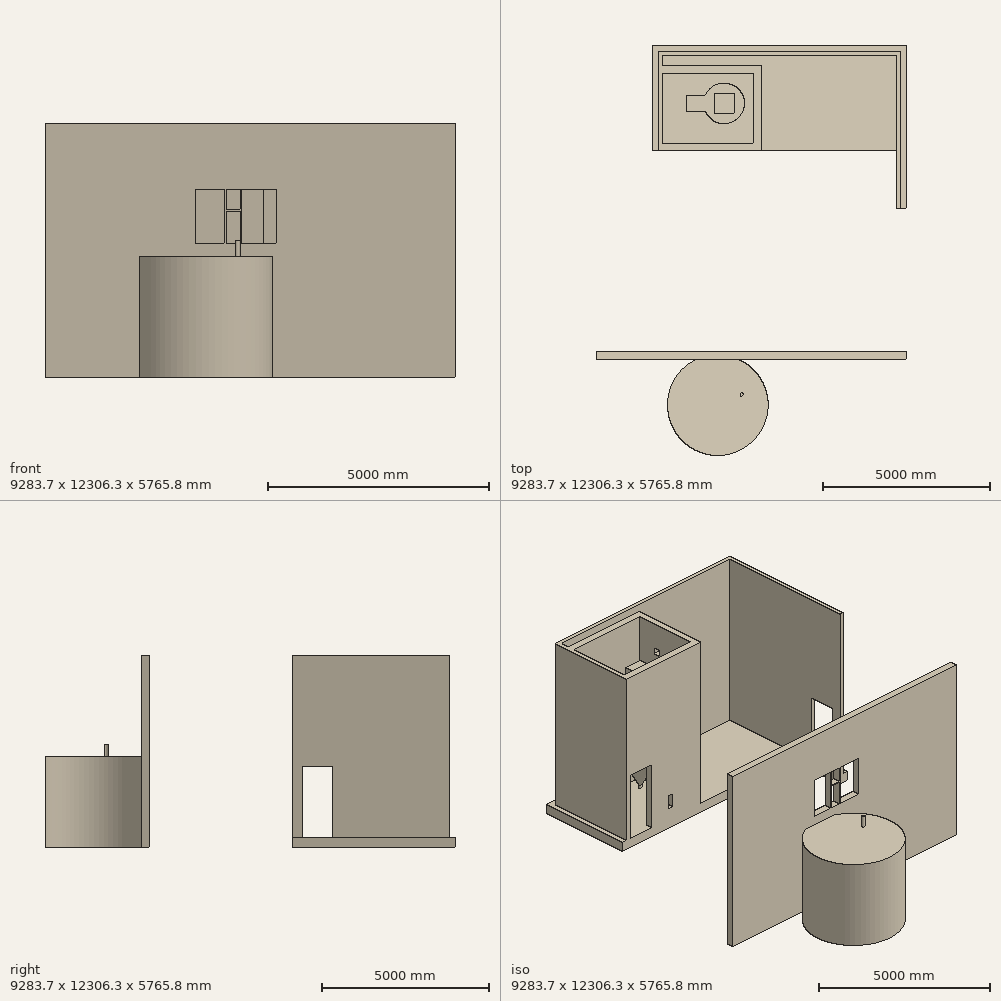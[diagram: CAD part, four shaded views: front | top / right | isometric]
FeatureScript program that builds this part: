
annotation { "Feature Type Name" : "Feature", "Feature Type Description" : "" }
export const myFeature = defineFeature(function(context is Context, id is Id, definition is map)
    precondition{}
    {
        {
            var Q0;
            Q0=qCreatedBy(makeId("Top.planeOp"),FACE);
            var sketch = newSketch(context, id + "F0", { "sketchPlane" : qUnion([Q0])});
            skLineSegment(sketch, "E0.bottom", {"start": v(-3263.9, 3149.6) * mm, "end": v(4051.3, 3149.6) * mm});
            skLineSegment(sketch, "E0.top", {"start": v(-3263.9, 0) * mm, "end": v(4051.3, 0) * mm});
            skLineSegment(sketch, "E0.left", {"start": v(-3263.9, 3149.6) * mm, "end": v(-3263.9, 0) * mm});
            skLineSegment(sketch, "E0.right", {"start": v(4051.3, 3149.6) * mm, "end": v(4051.3, 0) * mm});
            skLineSegment(sketch, "E1", {"start": v(4051.3, 0) * mm, "end": v(4051.3, -1727.2) * mm});
            skLineSegment(sketch, "E2", {"start": v(4051.3, -1727.2) * mm, "end": v(4356.1, -1727.2) * mm});
            skLineSegment(sketch, "E3", {"start": v(4356.1, -1727.2) * mm, "end": v(4356.1, 3149.6) * mm});
            skLineSegment(sketch, "E4", {"start": v(4356.1, 3149.6) * mm, "end": v(4051.3, 3149.6) * mm});
            skSolve(sketch);
        }
        {
            var Q0;
            Q0 = qSketchRegion(id + "F0", true);
            extrude(context, id + "F1", {"entities" : qUnion([Q0]), "depth" : 304.8 * mm, "offsetDistance" : 25.4 * mm});
        }
        {
            var Q0;
            Q0=makeQuery(id+"F1.opExtrude","CAP_FACE",FACE,{"disambiguationData":[OSD([sQuery(id+"F0.wireOp",EDGE,"E0.bottom"),sQuery(id+"F0.wireOp",EDGE,"E0.top"),sQuery(id+"F0.wireOp",EDGE,"E0.left"),sQuery(id+"F0.wireOp",EDGE,"E1"),sQuery(id+"F0.wireOp",EDGE,"E2"),sQuery(id+"F0.wireOp",EDGE,"E3"),sQuery(id+"F0.wireOp",EDGE,"E4")])],"isStart":false});
            var sketch = newSketch(context, id + "F2", { "sketchPlane" : qUnion([Q0])});
            skLineSegment(sketch, "E5", {"start": v(0, 0) * mm, "end": v(-2959.1, 0) * mm});
            skLineSegment(sketch, "E6", {"start": v(-2959.1, 0) * mm, "end": v(-2959.1, 2844.8) * mm});
            skLineSegment(sketch, "E7", {"start": v(-2959.1, 2844.8) * mm, "end": v(4051.3, 2844.8) * mm});
            skLineSegment(sketch, "E8", {"start": v(4051.3, 2844.8) * mm, "end": v(4051.3, -1727.2) * mm});
            skLineSegment(sketch, "E9", {"start": v(0, 0) * mm, "end": v(0, 2540) * mm});
            skLineSegment(sketch, "E10", {"start": v(0, 2540) * mm, "end": v(-2959.1, 2540) * mm});
            skLineSegment(sketch, "E11.0", {"start": v(4178.3, 2971.8) * mm, "end": v(4178.3, -1727.2) * mm});
            skLineSegment(sketch, "E11.1", {"start": v(-3086.1, 2971.8) * mm, "end": v(4178.3, 2971.8) * mm});
            skLineSegment(sketch, "E11.2", {"start": v(-3086.1, 0) * mm, "end": v(-3086.1, 2971.8) * mm});
            skLineSegment(sketch, "E12.0", {"start": v(-215.9, 215.9) * mm, "end": v(-2959.1, 215.9) * mm});
            skLineSegment(sketch, "E12.1", {"start": v(-215.9, 215.9) * mm, "end": v(-215.9, 2324.1) * mm});
            skLineSegment(sketch, "E12.2", {"start": v(-215.9, 2324.1) * mm, "end": v(-2959.1, 2324.1) * mm});
            skLineSegment(sketch, "E13", {"start": v(-3086.1, 0) * mm, "end": v(-2959.1, 0) * mm});
            skLineSegment(sketch, "E14", {"start": v(4178.3, -1727.2) * mm, "end": v(4051.3, -1727.2) * mm});
            skSolve(sketch);
        }
        {
            var Q0;
            Q0 = qSketchRegion(id + "F2", true);
            extrude(context, id + "F3", {"entities" : qUnion([Q0]), "operationType" : NewBodyOperationType.ADD, "depth" : 5461 * mm, "offsetDistance" : 25.4 * mm});
        }
        {
            var Q0;
            Q0=qCreatedBy(makeId("Top.planeOp"),FACE);
            var sketch = newSketch(context, id + "F4", { "sketchPlane" : qUnion([Q0])});
            skLineSegment(sketch, "E15.bottom", {"start": v(4356.1, -6032.5) * mm, "end": v(-4927.6, -6032.5) * mm});
            skLineSegment(sketch, "E15.top", {"start": v(4356.1, -6261.1) * mm, "end": v(-4927.6, -6261.1) * mm});
            skLineSegment(sketch, "E15.left", {"start": v(4356.1, -6032.5) * mm, "end": v(4356.1, -6261.1) * mm});
            skLineSegment(sketch, "E15.right", {"start": v(-4927.6, -6032.5) * mm, "end": v(-4927.6, -6261.1) * mm});
            skLineSegment(sketch, "E16", {"start": v(0, 0) * mm, "end": v(0, -6032.5) * mm, "construction": true});
            skSolve(sketch);
        }
        {
            var Q0;
            Q0 = qSketchRegion(id + "F4", true);
            extrude(context, id + "F5", {"entities" : qUnion([Q0]), "depth" : 5765.8 * mm, "offsetDistance" : 25.4 * mm});
        }
        {
            var Q0;
            Q0=makeQuery(id+"F5.opExtrude","SWEPT_FACE",FACE,{"disambiguationData":[OSD([sQuery(id+"F4.wireOp",EDGE,"E15.bottom")])]});
            var sketch = newSketch(context, id + "F6", { "sketchPlane" : qUnion([Q0])});
            skLineSegment(sketch, "E17.bottom", {"start": v(-304.8, 3048) * mm, "end": v(482.6, 3048) * mm});
            skLineSegment(sketch, "E17.top", {"start": v(-304.8, 4267.2) * mm, "end": v(482.6, 4267.2) * mm});
            skLineSegment(sketch, "E17.left", {"start": v(-304.8, 3048) * mm, "end": v(-304.8, 4267.2) * mm});
            skLineSegment(sketch, "E17.right", {"start": v(1524, 3048) * mm, "end": v(1524, 4267.2) * mm});
            skLineSegment(sketch, "E18", {"start": v(0, 0) * mm, "end": v(0, 3048) * mm, "construction": true});
            skLineSegment(sketch, "E19", {"start": v(482.6, 3048) * mm, "end": v(482.6, 4267.2) * mm});
            skLineSegment(sketch, "E20", {"start": v(863.6, 4267.2) * mm, "end": v(863.6, 3048) * mm});
            skLineSegment(sketch, "E21", {"start": v(520.7, 4267.2) * mm, "end": v(520.7, 3810) * mm});
            skLineSegment(sketch, "E22", {"start": v(520.7, 3810) * mm, "end": v(825.5, 3810) * mm});
            skLineSegment(sketch, "E23", {"start": v(825.5, 3810) * mm, "end": v(825.5, 4267.2) * mm});
            skLineSegment(sketch, "E24", {"start": v(520.7, 3048) * mm, "end": v(520.7, 3771.9) * mm});
            skLineSegment(sketch, "E25", {"start": v(520.7, 3771.9) * mm, "end": v(825.5, 3771.9) * mm});
            skLineSegment(sketch, "E26", {"start": v(825.5, 3771.9) * mm, "end": v(825.5, 3048) * mm});
            skLineSegment(sketch, "E27.trimOffspring", {"start": v(520.7, 4267.2) * mm, "end": v(825.5, 4267.2) * mm});
            skLineSegment(sketch, "E28.trimOffspring", {"start": v(863.6, 4267.2) * mm, "end": v(1524, 4267.2) * mm});
            skLineSegment(sketch, "E29.trimOffspring", {"start": v(520.7, 3048) * mm, "end": v(825.5, 3048) * mm});
            skLineSegment(sketch, "E30.trimOffspring", {"start": v(863.6, 3048) * mm, "end": v(1524, 3048) * mm});
            skLineSegment(sketch, "E31", {"start": v(825.5, 3409.95) * mm, "end": v(863.6, 3409.95) * mm, "construction": true});
            skLineSegment(sketch, "E32", {"start": v(520.7, 3409.95) * mm, "end": v(482.6, 3409.95) * mm, "construction": true});
            skLineSegment(sketch, "E33", {"start": v(825.5, 3810) * mm, "end": v(825.5, 3771.9) * mm, "construction": true});
            skSolve(sketch);
        }
        {
            var Q0;
            Q0 = qSketchRegion(id + "F6", true);
            extrude(context, id + "F7", {"entities" : qUnion([Q0]), "operationType" : NewBodyOperationType.REMOVE, "endBound" : BoundingType.UP_TO_NEXT, "oppositeDirection" : true, "depth" : 25.4 * mm, "offsetDistance" : 25.4 * mm});
        }
        {
            var Q0;
            Q0=makeQuery(id+"F3.boolean.opBoolean","MERGE",FACE,{"derivedFrom":[makeQuery(id+"F1.opExtrude","SWEPT_FACE",FACE,{"disambiguationData":[OSD([sQuery(id+"F0.wireOp",EDGE,"E0.top")])]}),makeQuery(id+"F3.opExtrude","SWEPT_FACE",FACE,{"disambiguationData":[OSD([sQuery(id+"F2.wireOp",EDGE,"E5"),sQuery(id+"F2.wireOp",EDGE,"E13")])]})]});
            var sketch = newSketch(context, id + "F8", { "sketchPlane" : qUnion([Q0])});
            skLineSegment(sketch, "E34.bottom", {"start": v(-2927.35, 304.8) * mm, "end": v(-2038.35, 304.8) * mm});
            skLineSegment(sketch, "E34.top", {"start": v(-2927.35, 2438.4) * mm, "end": v(-2038.35, 2438.4) * mm});
            skLineSegment(sketch, "E34.left", {"start": v(-2927.35, 304.8) * mm, "end": v(-2927.35, 2438.4) * mm});
            skLineSegment(sketch, "E34.right", {"start": v(-2038.35, 304.8) * mm, "end": v(-2038.35, 2438.4) * mm});
            skLineSegment(sketch, "E35.bottom", {"start": v(-1352.55, 660.4) * mm, "end": v(-1162.05, 660.4) * mm});
            skLineSegment(sketch, "E35.top", {"start": v(-1352.55, 1104.9) * mm, "end": v(-1162.05, 1104.9) * mm});
            skLineSegment(sketch, "E35.left", {"start": v(-1352.55, 660.4) * mm, "end": v(-1352.55, 1104.9) * mm});
            skLineSegment(sketch, "E35.right", {"start": v(-1162.05, 660.4) * mm, "end": v(-1162.05, 1104.9) * mm});
            skSolve(sketch);
        }
        {
            var Q0;
            Q0 = qSketchRegion(id + "F8", true);
            extrude(context, id + "F9", {"entities" : qUnion([Q0]), "operationType" : NewBodyOperationType.REMOVE, "endBound" : BoundingType.UP_TO_NEXT, "oppositeDirection" : true, "depth" : 25.4 * mm, "offsetDistance" : 25.4 * mm});
        }
        {
            var Q0;
            Q0=makeQuery(id+"F3.opExtrude","SWEPT_FACE",FACE,{"disambiguationData":[OSD([sQuery(id+"F2.wireOp",EDGE,"E11.0")])]});
            var sketch = newSketch(context, id + "F10", { "sketchPlane" : qUnion([Q0])});
            skLineSegment(sketch, "E36.bottom", {"start": v(-1435.1, 304.8) * mm, "end": v(-546.1, 304.8) * mm});
            skLineSegment(sketch, "E36.top", {"start": v(-1435.1, 2438.4) * mm, "end": v(-546.1, 2438.4) * mm});
            skLineSegment(sketch, "E36.left", {"start": v(-1435.1, 304.8) * mm, "end": v(-1435.1, 2438.4) * mm});
            skLineSegment(sketch, "E36.right", {"start": v(-546.1, 304.8) * mm, "end": v(-546.1, 2438.4) * mm});
            skSolve(sketch);
        }
        {
            var Q0;
            Q0 = qSketchRegion(id + "F10", true);
            extrude(context, id + "F11", {"entities" : qUnion([Q0]), "operationType" : NewBodyOperationType.REMOVE, "endBound" : BoundingType.UP_TO_NEXT, "oppositeDirection" : true, "depth" : 25.4 * mm, "offsetDistance" : 25.4 * mm});
        }
        {
            var Q0;
            Q0=makeQuery(id+"F3.opExtrude","SWEPT_FACE",FACE,{"disambiguationData":[OSD([sQuery(id+"F2.wireOp",EDGE,"E9")])]});
            var sketch = newSketch(context, id + "F12", { "sketchPlane" : qUnion([Q0])});
            skLineSegment(sketch, "E37.bottom", {"start": v(1244.6, 4241.8) * mm, "end": v(1663.7, 4241.8) * mm});
            skLineSegment(sketch, "E37.top", {"start": v(1244.6, 4013.2) * mm, "end": v(1663.7, 4013.2) * mm});
            skLineSegment(sketch, "E37.left", {"start": v(1244.6, 4241.8) * mm, "end": v(1244.6, 4013.2) * mm});
            skLineSegment(sketch, "E37.right", {"start": v(1663.7, 4241.8) * mm, "end": v(1663.7, 4013.2) * mm});
            skLineSegment(sketch, "E38.bottom", {"start": v(1511.3, 4965.7) * mm, "end": v(1714.5, 4965.7) * mm});
            skLineSegment(sketch, "E38.top", {"start": v(1511.3, 4762.5) * mm, "end": v(1714.5, 4762.5) * mm});
            skLineSegment(sketch, "E38.left", {"start": v(1511.3, 4965.7) * mm, "end": v(1511.3, 4762.5) * mm});
            skLineSegment(sketch, "E38.right", {"start": v(1714.5, 4965.7) * mm, "end": v(1714.5, 4762.5) * mm});
            skSolve(sketch);
        }
        {
            var Q0;
            Q0 = qSketchRegion(id + "F12", true);
            extrude(context, id + "F13", {"entities" : qUnion([Q0]), "operationType" : NewBodyOperationType.REMOVE, "endBound" : BoundingType.UP_TO_NEXT, "oppositeDirection" : true, "depth" : 25.4 * mm, "offsetDistance" : 25.4 * mm});
        }
        {
            var Q0;
            Q0=qCreatedBy(makeId("Top.planeOp"),FACE);
            var sketch = newSketch(context, id + "F14", { "sketchPlane" : qUnion([Q0])});
            skLineSegment(sketch, "E39", {"start": v(-1257.3, 0) * mm, "end": v(-431.4, -8851.55) * mm, "construction": true});
            skSolve(sketch);
        }
        {
            var Q0;
            Q0=qCreatedBy(makeId("Top.planeOp"),FACE);
            var sketch = newSketch(context, id + "F15", { "sketchPlane" : qUnion([Q0])});
            skCircle(sketch, "E40", {"center": v(-1294.11, -7645.4) * mm, "radius": 1511.3 * mm});
            skLineSegment(sketch, "E41", {"start": v(-1294.11, -7645.4) * mm, "end": v(-1294.11, -6134.1) * mm, "construction": true});
            skCircle(sketch, "E42", {"center": v(-573.56, -7327.9) * mm, "radius": 50.8 * mm, "construction": true});
            skLineSegment(sketch, "E43", {"start": v(-1294.11, -9156.7) * mm, "end": v(0, -9156.7) * mm, "construction": true});
            skSolve(sketch);
        }
        {
            var Q0;
            Q0 = qSketchRegion(id + "F15", true);
            extrude(context, id + "F16", {"entities" : qUnion([Q0]), "operationType" : NewBodyOperationType.ADD, "depth" : 2743.2 * mm, "offsetDistance" : 25.4 * mm});
        }
        {
            var Q0;
            Q0=makeQuery(id+"F16.opExtrude","CAP_FACE",FACE,{"disambiguationData":[OSD([sQuery(id+"F15.wireOp",EDGE,"E40")])],"isStart":false});
            var sketch = newSketch(context, id + "F17", { "sketchPlane" : qUnion([Q0])});
            skCircle(sketch, "E44", {"center": v(-573.56, -7327.9) * mm, "radius": 50.8 * mm});
            skSolve(sketch);
        }
        {
            var Q0;
            Q0 = qSketchRegion(id + "F17", true);
            extrude(context, id + "F18", {"entities" : qUnion([Q0]), "operationType" : NewBodyOperationType.ADD, "depth" : 355.6 * mm, "offsetDistance" : 25.4 * mm});
        }
        {
            var Q0;
            {var subQ0=sQuery(id+"F2.wireOp",EDGE,"E12.0");Q0=makeQuery(id+"F9.boolean.opBoolean","MERGE",FACE,{"derivedFrom":[makeQuery(id+"F3.boolean.opBoolean","SPLIT",FACE,{"disambiguationData":[TD([makeQuery(id+"F3.opExtrude","SWEPT_FACE",FACE,{"disambiguationData":[OSD([subQ0])]})])],"derivedFrom":makeQuery(id+"F1.opExtrude","CAP_FACE",FACE,{"disambiguationData":[OSD([sQuery(id+"F0.wireOp",EDGE,"E0.bottom"),sQuery(id+"F0.wireOp",EDGE,"E0.top"),sQuery(id+"F0.wireOp",EDGE,"E0.left"),sQuery(id+"F0.wireOp",EDGE,"E1"),sQuery(id+"F0.wireOp",EDGE,"E2"),sQuery(id+"F0.wireOp",EDGE,"E3"),sQuery(id+"F0.wireOp",EDGE,"E4")])],"isStart":false})})],"fromTools":[makeQuery(id+"F9.opExtrude","SWEPT_FACE",FACE,{"disambiguationData":[OSD([sQuery(id+"F8.wireOp",EDGE,"E34.bottom")])]})]});}
            cPlane(context, id + "F19", {"entities" : qUnion([Q0]), "cplaneType" : CPlaneType.OFFSET, "offset" : 2895.6 * mm, "width" : 152.4 * mm, "height" : 152.4 * mm});
        }
        {
            var Q0;
            Q0=qCreatedBy(id+"F19.planeOp",FACE);
            var sketch = newSketch(context, id + "F20", { "sketchPlane" : qUnion([Q0])});
            skLineSegment(sketch, "E45.bottom", {"start": v(-800.1, 1104.9) * mm, "end": v(-1409.7, 1104.9) * mm});
            skLineSegment(sketch, "E45.top", {"start": v(-800.1, 1714.5) * mm, "end": v(-1409.7, 1714.5) * mm});
            skLineSegment(sketch, "E45.left", {"start": v(-800.1, 1104.9) * mm, "end": v(-800.1, 1714.5) * mm});
            skLineSegment(sketch, "E45.right", {"start": v(-1409.7, 1104.9) * mm, "end": v(-1409.7, 1714.5) * mm});
            skPoint(sketch, "E45.middle", {"position": v(-1104.9, 1409.7) * mm});
            skSolve(sketch);
        }
        {
            var Q0;
            Q0 = qSketchRegion(id + "F20", true);
            extrude(context, id + "F21", {"entities" : qUnion([Q0]), "depth" : 1574.8 * mm, "offsetDistance" : 25.4 * mm});
        }
        {
            var Q0;
            Q0=makeQuery(id+"F21.opExtrude","CAP_FACE",FACE,{"disambiguationData":[OSD([sQuery(id+"F20.wireOp",EDGE,"E45.bottom"),sQuery(id+"F20.wireOp",EDGE,"E45.top"),sQuery(id+"F20.wireOp",EDGE,"E45.left"),sQuery(id+"F20.wireOp",EDGE,"E45.right")])],"isStart":true});
            var sketch = newSketch(context, id + "F22", { "sketchPlane" : qUnion([Q0])});
            skCircle(sketch, "E46", {"center": v(-1104.9, -1409.7) * mm, "radius": 609.6 * mm});
            skLineSegment(sketch, "E47", {"start": v(-1104.9, -1409.7) * mm, "end": v(-1714.5, -1409.7) * mm, "construction": true});
            skPoint(sketch, "E47.endSnap0", {"position": v(-1409.7, -1409.7) * mm});
            skSolve(sketch);
        }
        {
            var Q0;
            Q0 = qSketchRegion(id + "F22", true);
            extrude(context, id + "F23", {"entities" : qUnion([Q0]), "operationType" : NewBodyOperationType.ADD, "depth" : 1346.2 * mm, "offsetDistance" : 25.4 * mm});
        }
        {
            var Q0;
            Q0=makeQuery(id+"F3.opExtrude","SWEPT_FACE",FACE,{"disambiguationData":[OSD([sQuery(id+"F2.wireOp",EDGE,"E12.2")])]});
            cPlane(context, id + "F24", {"entities" : qUnion([Q0]), "cplaneType" : CPlaneType.OFFSET, "offset" : 914.4 * mm, "width" : 152.4 * mm, "height" : 152.4 * mm});
        }
        {
            var Q0;
            Q0=qCreatedBy(id+"F24.planeOp",FACE);
            var sketch = newSketch(context, id + "F25", { "sketchPlane" : qUnion([Q0])});
            skLineSegment(sketch, "E48", {"start": v(-1104.9, 1854.2) * mm, "end": v(-1104.9, 812.8) * mm});
            skLineSegment(sketch, "E49", {"start": v(-1104.9, 812.8) * mm, "end": v(-1155.7, 812.8) * mm});
            skLineSegment(sketch, "E50", {"start": v(-1155.7, 812.8) * mm, "end": v(-1714.5, 1854.2) * mm});
            skLineSegment(sketch, "E51", {"start": v(-1714.5, 1854.2) * mm, "end": v(-1104.9, 1854.2) * mm});
            skSolve(sketch);
        }
        {
            var Q0;
            Q0 = qSketchRegion(id + "F25", true);
            var Q1;
            Q1=sQuery(id+"F25.wireOp",EDGE,"E48");
            revolve(context, id + "F26", {"operationType" : NewBodyOperationType.ADD, "surfaceOperationType" : NewSurfaceOperationType.NEW, "entities" : qUnion([Q0]), "axis" : qUnion([Q1]), "revolveType" : RevolveType.FULL});
        }
        {
            var Q0;
            Q0=makeQuery(id+"F26.opRevolve","SWEPT_FACE",FACE,{"disambiguationData":[OSD([sQuery(id+"F25.wireOp",EDGE,"E49")])]});
            var sketch = newSketch(context, id + "F27", { "sketchPlane" : qUnion([Q0])});
            skCircle(sketch, "E52", {"center": v(-1104.9, -1409.7) * mm, "radius": 50.8 * mm});
            skSolve(sketch);
        }
        {
            var Q0;
            Q0 = qSketchRegion(id + "F27", true);
            extrude(context, id + "F28", {"entities" : qUnion([Q0]), "operationType" : NewBodyOperationType.ADD, "depth" : 101.6 * mm, "offsetDistance" : 25.4 * mm});
        }
        {
            var Q0;
            Q0=qCreatedBy(id+"F24.planeOp",FACE);
            var sketch = newSketch(context, id + "F29", { "sketchPlane" : qUnion([Q0])});
            skLineSegment(sketch, "E53", {"start": v(-1409.7, 1867.03) * mm, "end": v(-2222.5, 2692.4) * mm});
            skLineSegment(sketch, "E54", {"start": v(-2222.5, 2692.4) * mm, "end": v(-2222.5, 3200.4) * mm});
            skLineSegment(sketch, "E55", {"start": v(-2222.5, 3200.4) * mm, "end": v(-1409.7, 3200.4) * mm});
            skLineSegment(sketch, "E56", {"start": v(-1409.7, 3200.4) * mm, "end": v(-1409.7, 1867.03) * mm});
            skSolve(sketch);
        }
        {
            var Q0;
            Q0 = qSketchRegion(id + "F29", true);
            extrude(context, id + "F30", {"entities" : qUnion([Q0]), "operationType" : NewBodyOperationType.ADD, "endBound" : BoundingType.SYMMETRIC, "depth" : 508 * mm, "offsetDistance" : 25.4 * mm});
        }
    });
